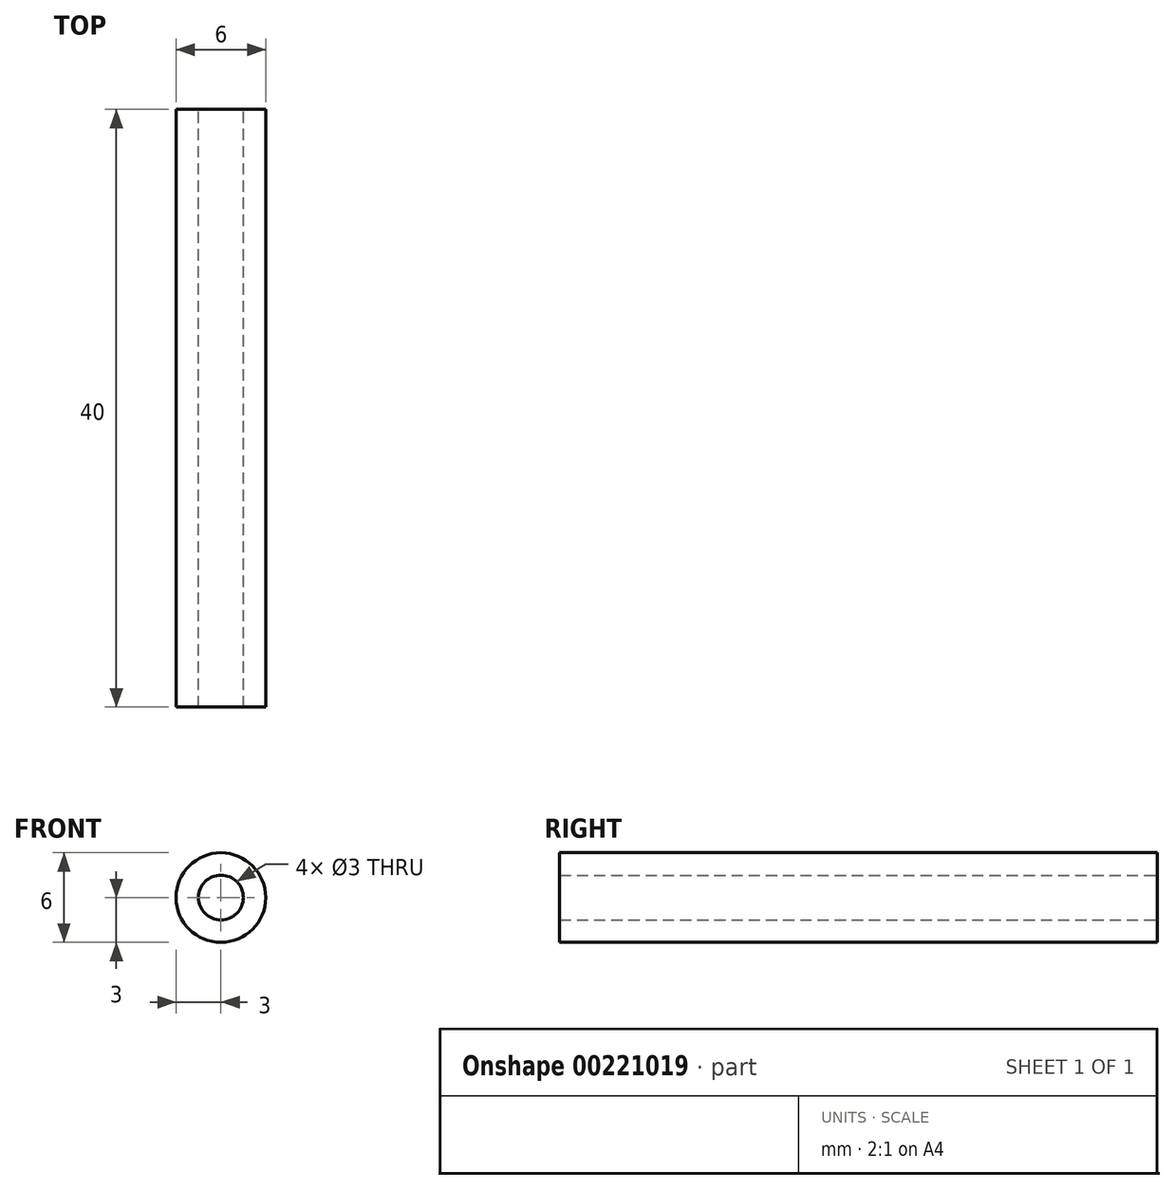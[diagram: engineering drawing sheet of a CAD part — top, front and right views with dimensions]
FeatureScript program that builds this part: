
annotation { "Feature Type Name" : "Feature", "Feature Type Description" : "" }
export const myFeature = defineFeature(function(context is Context, id is Id, definition is map)
    precondition{}
    {
        {
            var Q0;
            Q0=qCreatedBy(makeId("Front.planeOp"),FACE);
            var sketch = newSketch(context, id + "F0", { "sketchPlane" : qUnion([Q0])});
            skCircle(sketch, "E0", {"center": v(0, 0) * mm, "radius": 1.5 * mm});
            skCircle(sketch, "E1", {"center": v(0, 0) * mm, "radius": 3 * mm});
            skSolve(sketch);
        }
        {
            var Q0;
            Q0 = qSketchRegion(id + "F0", true);
            extrude(context, id + "F1", {"entities" : qUnion([Q0]), "depth" : 40 * mm});
        }
    });
